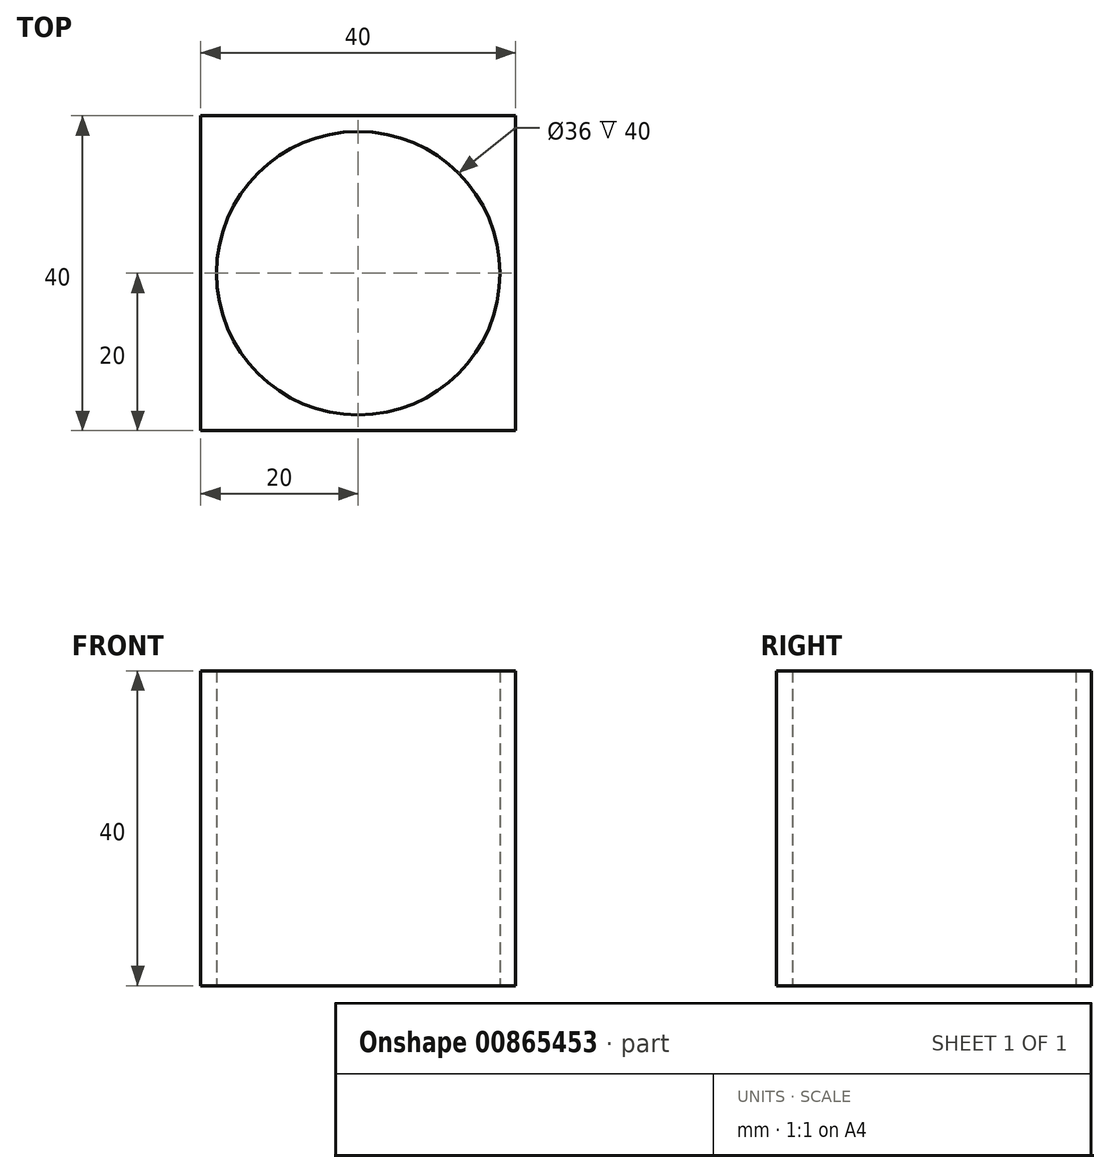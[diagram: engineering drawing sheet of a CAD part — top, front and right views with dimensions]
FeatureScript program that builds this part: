
annotation { "Feature Type Name" : "Feature", "Feature Type Description" : "" }
export const myFeature = defineFeature(function(context is Context, id is Id, definition is map)
    precondition{}
    {
        {
            var Q0;
            Q0=qCreatedBy(makeId("Top.planeOp"),FACE);
            var sketch = newSketch(context, id + "F0", { "sketchPlane" : qUnion([Q0])});
            skLineSegment(sketch, "E0.bottom", {"start": v(20, 20) * mm, "end": v(-20, 20) * mm});
            skLineSegment(sketch, "E0.top", {"start": v(20, -20) * mm, "end": v(-20, -20) * mm});
            skLineSegment(sketch, "E0.left", {"start": v(20, 20) * mm, "end": v(20, -20) * mm});
            skLineSegment(sketch, "E0.right", {"start": v(-20, 20) * mm, "end": v(-20, -20) * mm});
            skPoint(sketch, "E0.middle", {"position": v(0, 0) * mm});
            skCircle(sketch, "E1", {"center": v(0, 0) * mm, "radius": 18 * mm});
            skSolve(sketch);
        }
        {
            var Q0;
            Q0 = qSketchRegion(id + "F0", true);
            extrude(context, id + "F1", {"entities" : qUnion([Q0]), "depth" : 40 * mm, "offsetDistance" : 25 * mm});
        }
    });
